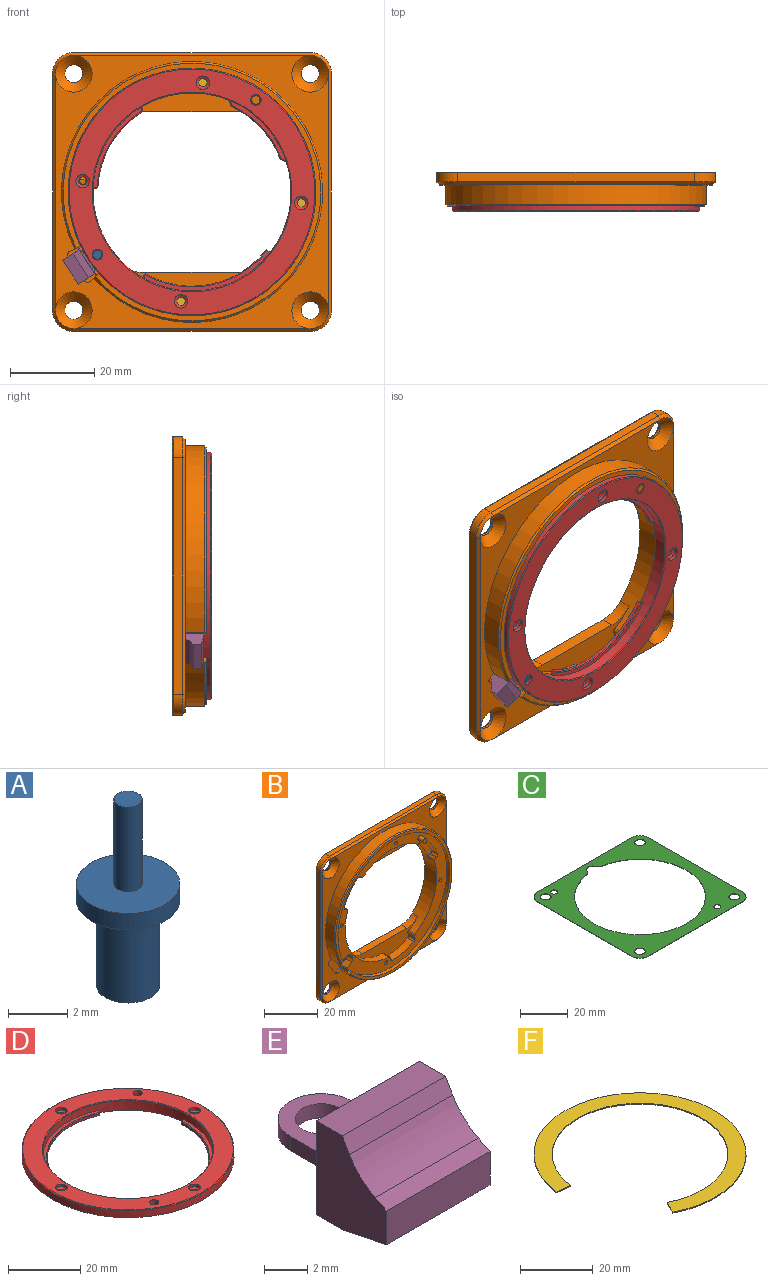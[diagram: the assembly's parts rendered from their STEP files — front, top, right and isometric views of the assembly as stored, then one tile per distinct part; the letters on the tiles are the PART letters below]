
ASSEMBLY  parts=6 mates=6
PART A: 7 faces, bbox 3.5x3.5x7.7 mm
  f0: cylinder r=1.07mm len=3.5mm, axis (0,0,-1), area 23.6mm2, adj f1,f4
  f1: plane 2.15x2.15mm, normal (0,0,-1), area 3.6mm2, adj f0
  f2: cylinder r=1.75mm len=3.5mm, axis (0,0,-1), area 7.5mm2, adj f3,f4
  f3: plane 3.5x3.5mm, normal (0,0,1), area 8.9mm2, adj f2,f5
  f4: plane 3.5x3.5mm, normal (0,0,-1), area 6mm2, adj f0,f2
  f5: cylinder r=0.47mm len=3.5mm, axis (0,0,-1), area 10.4mm2, adj f3,f6
  f6: plane 0.95x0.95mm, normal (0,0,1), area 0.7mm2, adj f5
PART B: 132 faces, bbox 66x9x66 mm
  f0: plane 66x66mm, normal (0,1,0), area 1941mm2, adj f7,f8,f9,f10,f11,f12,f13,f14
  f1: plane 64.6x64.6mm, normal (0,-1,0), area 904mm2, adj f2,f20,f21,f22,f23,f25,f26,f29
  f2: cylinder r=30.9mm len=61.8mm, axis (0,1,0), area 845.7mm2, adj f1,f54,f55,f84
  f3: plane 58.65x58.65mm, normal (0,-1,0), area 755.9mm2, adj f4,f5,f6,f40,f42,f44,f46,f48
  f4: cylinder r=24.05mm len=40.58mm, axis (0,1,0), area 255.6mm2, adj f3,f19,f33,f35,f37,f38,f67,f75
  f5: cylinder r=24.05mm len=37.04mm, axis (0,1,0), area 215.4mm2, adj f3,f19,f33,f35,f36,f39,f66,f70
  f6: cylinder r=24.05mm len=28.41mm, axis (0,1,0), area 100.3mm2, adj f3,f35,f72,f77
  f7: plane 56x2.15mm, normal (0,0,-1), area 120.4mm2, adj f0,f8,f14,f29
  f8: cylinder r=5mm len=5mm, axis (0,1,0), area 16.9mm2, adj f0,f7,f9,f31
  f9: plane 56x2.15mm, normal (1,0,0), area 120.4mm2, adj f0,f8,f10,f30
  f10: cylinder r=5mm len=5mm, axis (0,1,0), area 16.9mm2, adj f0,f9,f11,f28
  f11: plane 56x2.15mm, normal (0,0,1), area 120.4mm2, adj f0,f10,f12,f26
  f12: cylinder r=5mm len=5mm, axis (0,1,0), area 16.9mm2, adj f0,f11,f13,f24
  f13: plane 56x2.15mm, normal (-1,0,0), area 120.4mm2, adj f0,f12,f14,f25
  f14: cylinder r=5mm len=5mm, axis (0,1,0), area 16.9mm2, adj f0,f7,f13,f27
  f15: cylinder r=2.15mm len=4.3mm, axis (0,1,0), area 8.8mm2, adj f0,f22
  f16: cylinder r=2.15mm len=4.3mm, axis (0,1,0), area 8.8mm2, adj f0,f23
  f17: cylinder r=2.15mm len=4.3mm, axis (0,1,0), area 8.8mm2, adj f0,f20
  f18: cylinder r=2.15mm len=4.3mm, axis (0,1,0), area 8.8mm2, adj f0,f21
  f19: plane 49.6x39.6mm, normal (0,1,0), area 336.2mm2, adj f4,f5,f32,f34,f36,f37,f38,f39
  f20: cone r=2.15mm half-angle=45deg, axis (0,-1,0), area 63.3mm2, adj f1,f17,f29,f30,f31
  f21: cone r=4.35mm half-angle=45deg, axis (0,-1,0), area 63.3mm2, adj f1,f18,f25,f27,f29
  f22: cone r=2.15mm half-angle=45deg, axis (0,-1,0), area 63.3mm2, adj f1,f15,f24,f25,f26
  f23: cone r=4.35mm half-angle=45deg, axis (0,-1,0), area 63.3mm2, adj f1,f16,f26,f28,f30
  f24: cone r=4.3mm half-angle=45deg, axis (0,1,0), area 7mm2, adj f12,f22,f25,f26
  f25: plane 56.02x0.72mm, normal (-0.71,-0.71,0), area 55.4mm2, adj f1,f13,f21,f22,f24,f27
  f26: plane 56.02x0.72mm, normal (0,-0.71,0.71), area 55.4mm2, adj f1,f11,f22,f23,f24,f28
  f27: cone r=4.3mm half-angle=45deg, axis (0,1,0), area 7mm2, adj f14,f21,f25,f29
  f28: cone r=4.3mm half-angle=45deg, axis (0,1,0), area 7mm2, adj f10,f23,f26,f30
  f29: plane 56.02x0.72mm, normal (0,-0.71,-0.71), area 55.4mm2, adj f1,f7,f20,f21,f27,f31
  f30: plane 56.02x0.72mm, normal (0.71,-0.71,0), area 55.4mm2, adj f1,f9,f20,f23,f28,f31
  f31: cone r=4.3mm half-angle=45deg, axis (0,1,0), area 7mm2, adj f8,f20,f29,f30
  f32: plane 23.28x3mm, normal (0,0,1), area 69.8mm2, adj f19,f33,f36,f37
  f33: plane 34.89x9.93mm, normal (0,-1,0), area 134.9mm2, adj f4,f5,f32,f36,f37,f57,f58,f59
  f34: plane 23.28x3mm, normal (0,0,-1), area 69.8mm2, adj f19,f35,f38,f39
  f35: plane 49.03x16.61mm, normal (0,-1,0), area 169.4mm2, adj f4,f5,f6,f34,f38,f39,f60,f61
  f36: cylinder r=8mm len=5.8mm, axis (0,1,0), area 19.5mm2, adj f5,f19,f32,f33
  f37: cylinder r=8mm len=5.8mm, axis (0,1,0), area 19.5mm2, adj f4,f19,f32,f33
  f38: cylinder r=8mm len=5.8mm, axis (0,1,0), area 19.5mm2, adj f4,f19,f34,f35
  f39: cylinder r=8mm len=5.8mm, axis (0,1,0), area 19.5mm2, adj f5,f19,f34,f35
  f40: cylinder r=0.75mm len=3mm, axis (0,-1,0), area 14.1mm2, adj f3,f41
  f41: plane 1.5x1.5mm, normal (0,-1,0), area 1.8mm2, adj f40
  f42: cylinder r=0.75mm len=3mm, axis (0,-1,0), area 14.1mm2, adj f3,f43
  f43: plane 1.5x1.5mm, normal (0,-1,0), area 1.8mm2, adj f42
  f44: cylinder r=0.75mm len=3mm, axis (0,-1,0), area 14.1mm2, adj f3,f45
  f45: plane 1.5x1.5mm, normal (0,-1,0), area 1.8mm2, adj f44
  f46: cylinder r=0.75mm len=3mm, axis (0,-1,0), area 14.1mm2, adj f3,f47
  f47: plane 1.5x1.5mm, normal (0,-1,0), area 1.8mm2, adj f46
  f48: plane 4.2x2.21mm, normal (-0.62,0,0.78), area 11.9mm2, adj f3,f49,f79,f85
  f49: cylinder r=2mm len=4.2mm, axis (0,-1,0), area 12.5mm2, adj f3,f48,f50,f85
  f50: plane 4.2x0.53mm, normal (-0.83,0,-0.55), area 2.7mm2, adj f3,f49,f51,f85
  f51: cylinder r=2mm len=4.2mm, axis (0,-1,0), area 12.5mm2, adj f3,f50,f52,f85
  f52: plane 4.2x2.48mm, normal (0.48,0,-0.88), area 11.9mm2, adj f3,f51,f78,f85
  f53: plane 4.2x0.42mm, normal (-0.83,0,-0.55), area 2.1mm2, adj f3,f78,f81,f85
  f54: plane 5.7x2.46mm, normal (0.44,0,-0.9), area 5.2mm2, adj f1,f2,f3,f81,f82,f83,f84,f85
  f55: plane 5.7x2.05mm, normal (-0.66,0,0.75), area 5.2mm2, adj f1,f2,f3,f80,f82,f83,f84,f85
  f56: plane 4.2x0.42mm, normal (-0.83,0,-0.55), area 2.1mm2, adj f3,f79,f80,f85
  f57: plane 3.3x0.39mm, normal (-0.87,0,-0.49), area 1.5mm2, adj f3,f33,f66,f68
  f58: plane 3.3x0.45mm, normal (1,0,-0.01), area 1.5mm2, adj f3,f33,f67,f69
  f59: cylinder r=26.5mm len=11.34mm, axis (0,-1,0), area 38.9mm2, adj f3,f33,f68,f69
  f60: plane 3.3x0.42mm, normal (-0.35,0,0.94), area 1.5mm2, adj f3,f35,f70,f71
  f61: cylinder r=26.5mm len=10.15mm, axis (0,-1,0), area 42mm2, adj f3,f35,f71,f73
  f62: plane 3.3x0.36mm, normal (0.79,0,-0.61), area 1.5mm2, adj f3,f35,f72,f73
  f63: cylinder r=26.5mm len=9.5mm, axis (0,-1,0), area 38.9mm2, adj f3,f35,f74,f76
  f64: plane 3.3x0.42mm, normal (0.35,0,0.94), area 1.5mm2, adj f3,f35,f74,f75
  f65: plane 3.3x0.35mm, normal (-0.77,0,-0.63), area 1.5mm2, adj f3,f35,f76,f77
  f66: cylinder r=1mm len=3.3mm, axis (0,1,0), area 5.1mm2, adj f3,f5,f33,f57
  f67: cylinder r=1mm len=3.3mm, axis (0,1,0), area 5.1mm2, adj f3,f4,f33,f58
  f68: cylinder r=1mm len=3.3mm, axis (0,-1,0), area 5.3mm2, adj f3,f33,f57,f59
  f69: cylinder r=1mm len=3.3mm, axis (0,-1,0), area 5.3mm2, adj f3,f33,f58,f59
  f70: cylinder r=1mm len=3.3mm, axis (0,1,0), area 5.1mm2, adj f3,f5,f35,f60
  f71: cylinder r=1mm len=3.3mm, axis (0,-1,0), area 5.3mm2, adj f3,f35,f60,f61
  f72: cylinder r=1mm len=3.3mm, axis (0,1,0), area 5.1mm2, adj f3,f6,f35,f62
  f73: cylinder r=1mm len=3.3mm, axis (0,-1,0), area 5.3mm2, adj f3,f35,f61,f62
  f74: cylinder r=1mm len=3.3mm, axis (0,-1,0), area 5.3mm2, adj f3,f35,f63,f64
  f75: cylinder r=1mm len=3.3mm, axis (0,1,0), area 5.1mm2, adj f3,f4,f35,f64
  f76: cylinder r=1mm len=3.3mm, axis (0,-1,0), area 5.3mm2, adj f3,f35,f63,f65
  f77: cylinder r=1mm len=3.3mm, axis (0,1,0), area 5.1mm2, adj f3,f6,f35,f65
  f78: cylinder r=0.5mm len=4.2mm, axis (0,1,0), area 3.1mm2, adj f3,f52,f53,f85
  f79: cylinder r=0.5mm len=4.2mm, axis (0,1,0), area 3.1mm2, adj f3,f48,f56,f85
  f80: cylinder r=0.5mm len=4.2mm, axis (0,1,0), area 3mm2, adj f3,f55,f56,f85
  f81: cylinder r=0.5mm len=4.2mm, axis (0,-1,0), area 3mm2, adj f3,f53,f54,f85
  f82: cylinder r=29.32mm len=58.65mm, axis (0,1,0), area 264.6mm2, adj f3,f54,f55,f83
  f83: plane 61x61mm, normal (0,-1,0), area 211.4mm2, adj f54,f55,f82,f84
  f84: cone r=30.5mm half-angle=45deg, axis (0,1,0), area 104.5mm2, adj f2,f54,f55,f83
  f85: plane 9.41x8.93mm, normal (0,-1,0), area 45.7mm2, adj f48,f49,f50,f51,f52,f53,f54,f55
  f86: cylinder r=1mm len=1.45mm, axis (0,-1,0), area 1.3mm2, adj f1,f54,f85,f87
  f87: plane 5.48x3.63mm, normal (0.83,0,0.55), area 4.9mm2, adj f1,f85,f86,f88
  f88: cylinder r=1mm len=1.49mm, axis (0,-1,0), area 1.3mm2, adj f1,f55,f85,f87
  f89: cylinder r=0.55mm len=3.5mm, axis (0,-1,0), area 12.1mm2, adj f90,f131
  f90: plane 2.1x2.1mm, normal (0,-1,0), area 2.5mm2, adj f89,f91
  f91: cylinder r=1.05mm len=2.2mm, axis (0,-1,0), area 14.5mm2, adj f85,f90
  f92: cylinder r=1.5mm len=3mm, axis (0,1,0), area 10.4mm2, adj f0,f93
  f93: plane 3x3mm, normal (0,1,0), area 7.1mm2, adj f92
  f94: cylinder r=1.5mm len=3mm, axis (0,1,0), area 10.4mm2, adj f0,f95
  f95: plane 3x3mm, normal (0,1,0), area 7.1mm2, adj f94
  f96: plane 41x0.9mm, normal (0,0,-1), area 36.9mm2, adj f104,f109,f112,f123
  f97: plane 31x0.9mm, normal (-1,0,0), area 27.9mm2, adj f104,f109,f110,f127
  f98: plane 41x0.9mm, normal (0,0,1), area 36.9mm2, adj f104,f110,f111,f126
  f99: plane 41x0.9mm, normal (0,0,1), area 36.9mm2, adj f104,f105,f108,f114
  f100: plane 31x0.9mm, normal (-1,0,0), area 27.9mm2, adj f104,f105,f106,f115
  f101: plane 41x0.9mm, normal (0,0,-1), area 36.9mm2, adj f104,f106,f107,f119
  f102: plane 31x0.9mm, normal (1,0,0), area 27.9mm2, adj f104,f107,f108,f118
  f103: plane 31x0.9mm, normal (1,0,0), area 27.9mm2, adj f104,f111,f112,f122
  f104: plane 53x43mm, normal (0,1,0), area 230.9mm2, adj f96,f97,f98,f99,f100,f101,f102,f103
  f105: cylinder r=4.7mm len=4.7mm, axis (0,1,0), area 6.6mm2, adj f99,f100,f104,f113
  f106: cylinder r=4.7mm len=4.7mm, axis (0,-1,0), area 6.6mm2, adj f100,f101,f104,f117
  f107: cylinder r=4.7mm len=4.7mm, axis (0,1,0), area 6.6mm2, adj f101,f102,f104,f120
  f108: cylinder r=4.7mm len=4.7mm, axis (0,-1,0), area 6.6mm2, adj f99,f102,f104,f116
  f109: cylinder r=6mm len=6mm, axis (0,1,0), area 8.5mm2, adj f96,f97,f104,f125
  f110: cylinder r=6mm len=6mm, axis (0,-1,0), area 8.5mm2, adj f97,f98,f104,f128
  f111: cylinder r=6mm len=6mm, axis (0,1,0), area 8.5mm2, adj f98,f103,f104,f124
  f112: cylinder r=6mm len=6mm, axis (0,-1,0), area 8.5mm2, adj f96,f103,f104,f121
  f113: cone r=4.3mm half-angle=45deg, axis (0,-1,0), area 4mm2, adj f19,f105,f114,f115
  f114: plane 41x0.4mm, normal (0,0.71,0.71), area 23.2mm2, adj f19,f99,f113,f116
  f115: plane 31x0.4mm, normal (-0.71,0.71,0), area 17.5mm2, adj f19,f100,f113,f117
  f116: cone r=4.3mm half-angle=45deg, axis (0,-1,0), area 4mm2, adj f19,f108,f114,f118
  f117: cone r=4.3mm half-angle=45deg, axis (0,-1,0), area 4mm2, adj f19,f106,f115,f119
  f118: plane 31x0.4mm, normal (0.71,0.71,0), area 17.5mm2, adj f19,f102,f116,f120
  f119: plane 41x0.4mm, normal (0,0.71,-0.71), area 23.2mm2, adj f19,f101,f117,f120
  f120: cone r=4.3mm half-angle=45deg, axis (0,-1,0), area 4mm2, adj f19,f107,f118,f119
  f121: cone r=6.4mm half-angle=45deg, axis (0,1,0), area 5.5mm2, adj f0,f112,f122,f123
  f122: plane 31x0.4mm, normal (0.71,0.71,0), area 17.5mm2, adj f0,f103,f121,f124
  f123: plane 41x0.4mm, normal (0,0.71,-0.71), area 23.2mm2, adj f0,f96,f121,f125
  f124: cone r=6.4mm half-angle=45deg, axis (0,1,0), area 5.5mm2, adj f0,f111,f122,f126
  f125: cone r=6.4mm half-angle=45deg, axis (0,1,0), area 5.5mm2, adj f0,f109,f123,f127
  f126: plane 41x0.4mm, normal (0,0.71,0.71), area 23.2mm2, adj f0,f98,f124,f128
  f127: plane 31x0.4mm, normal (-0.71,0.71,0), area 17.5mm2, adj f0,f97,f125,f128
  f128: cone r=6.4mm half-angle=45deg, axis (0,1,0), area 5.5mm2, adj f0,f110,f126,f127
  f129: cylinder r=1mm len=2.7mm, axis (0,1,0), area 17mm2, adj f3,f130
  f130: plane 2x2mm, normal (0,-1,0), area 3.1mm2, adj f129
  f131: plane 1.1x1.1mm, normal (0,-1,0), area 1mm2, adj f89
PART C: 20 faces, bbox 65.9x65.9x0.2 mm
  f0: plane 55.9x0.15mm, normal (0,-1,0), area 8.4mm2, adj f1,f17,f18,f19
  f1: cylinder r=5mm len=5mm, axis (0,0,-1), area 1.2mm2, adj f0,f2,f18,f19
  f2: plane 55.9x0.15mm, normal (1,0,0), area 8.4mm2, adj f1,f3,f18,f19
  f3: cylinder r=5mm len=5mm, axis (0,0,-1), area 1.2mm2, adj f2,f4,f18,f19
  f4: plane 55.9x0.15mm, normal (0,1,0), area 8.4mm2, adj f3,f5,f18,f19
  f5: cylinder r=5mm len=5mm, axis (0,0,-1), area 1.2mm2, adj f4,f6,f18,f19
  f6: plane 55.9x0.15mm, normal (-1,0,0), area 8.4mm2, adj f5,f17,f18,f19
  f7: cylinder r=2.65mm len=4.76mm, axis (0,0,-1), area 0.9mm2, adj f8,f16,f18,f19
  f8: cylinder r=4mm len=2.83mm, axis (0,0,-1), area 0.6mm2, adj f7,f9,f18,f19
  f9: cylinder r=27.5mm len=55mm, axis (0,0,-1), area 24.3mm2, adj f8,f16,f18,f19
  f10: cylinder r=2.25mm len=4.5mm, axis (0,0,-1), area 2.1mm2, adj f18,f19
  f11: cylinder r=2.25mm len=4.5mm, axis (0,0,-1), area 2.1mm2, adj f18,f19
  f12: cylinder r=2.25mm len=4.5mm, axis (0,0,-1), area 2.1mm2, adj f18,f19
  f13: cylinder r=1.5mm len=3mm, axis (0,0,-1), area 1.4mm2, adj f18,f19
  f14: cylinder r=1.5mm len=3mm, axis (0,0,-1), area 1.4mm2, adj f18,f19
  f15: cylinder r=2.25mm len=4.5mm, axis (0,0,-1), area 2.1mm2, adj f18,f19
  f16: cylinder r=4mm len=2.83mm, axis (0,0,-1), area 0.6mm2, adj f7,f9,f18,f19
  f17: cylinder r=5mm len=5mm, axis (0,0,-1), area 1.2mm2, adj f0,f6,f18,f19
  f18: plane 65.9x65.9mm, normal (0,0,1), area 1851.8mm2, adj f0,f1,f2,f3,f4,f5,f6,f7
  f19: plane 65.9x65.9mm, normal (0,0,-1), area 1851.8mm2, adj f0,f1,f2,f3,f4,f5,f6,f7
PART D: 48 faces, bbox 58.6x58.6x3.4 mm
  f0: cylinder r=1.25mm len=2.5mm, axis (0,0,-1), area 14.9mm2, adj f9,f47
  f1: plane 58.6x58.6mm, normal (0,0,-1), area 827.8mm2, adj f2,f3,f4,f5,f7,f8,f22,f43
  f2: cylinder r=1mm len=2mm, axis (0,0,-1), area 7.8mm2, adj f1,f39
  f3: cylinder r=1mm len=2mm, axis (0,0,-1), area 7.8mm2, adj f1,f41
  f4: cylinder r=1mm len=2mm, axis (0,0,-1), area 7.8mm2, adj f1,f35
  f5: cylinder r=1mm len=2mm, axis (0,0,-1), area 7.8mm2, adj f1,f37
  f6: cylinder r=23.45mm len=46.9mm, axis (0,0,-1), area 401.1mm2, adj f10,f11,f12,f14,f15,f17,f18,f20
  f7: cylinder r=1.25mm len=2.5mm, axis (0,0,-1), area 19.6mm2, adj f1,f9
  f8: cylinder r=29.3mm len=58.6mm, axis (0,0,-1), area 418.6mm2, adj f1,f33,f44,f45,f47
  f9: plane 58.2x58.2mm, normal (0,0,1), area 861.2mm2, adj f0,f7,f33,f34,f36,f38,f40,f42
  f10: plane 29.17x11.36mm, normal (0,0,1), area 30.9mm2, adj f6,f27,f28,f29
  f11: plane 14.61x12.93mm, normal (0,0,1), area 17.9mm2, adj f6,f30,f31,f32
  f12: plane 20.42x9.69mm, normal (0,0,1), area 21.4mm2, adj f6,f24,f25,f26
  f13: cylinder r=22.3mm len=12.78mm, axis (0,0,1), area 12.3mm2, adj f14,f21,f23,f31
  f14: plane 1.43x0.7mm, normal (0.9,0.44,0), area 1.1mm2, adj f6,f13,f23,f30
  f15: plane 1.58x0.7mm, normal (-0.99,0.12,0), area 1.1mm2, adj f6,f16,f23,f25
  f16: cylinder r=22.3mm len=18.83mm, axis (0,0,1), area 15mm2, adj f15,f17,f23,f26
  f17: plane 1.13x0.7mm, normal (-0.31,0.95,0), area 0.8mm2, adj f6,f16,f23,f24
  f18: plane 1.05x0.7mm, normal (0.91,-0.41,0), area 0.8mm2, adj f6,f19,f23,f28
  f19: cylinder r=22.3mm len=28.02mm, axis (0,0,1), area 22.4mm2, adj f18,f20,f23,f29
  f20: plane 0.98x0.7mm, normal (-0.53,-0.85,0), area 0.8mm2, adj f6,f19,f23,f27
  f21: plane 1.5x0.7mm, normal (0.33,0.95,0), area 1.1mm2, adj f6,f13,f23,f32
  f22: cylinder r=24mm len=48mm, axis (0,0,1), area 139.8mm2, adj f1,f23,f43,f46,f47
  f23: plane 48x48mm, normal (0,0,-1), area 167.8mm2, adj f6,f13,f14,f15,f16,f17,f18,f19
  f24: cylinder r=0.2mm len=1.19mm, axis (0.95,0.31,0), area 0.4mm2, adj f6,f12,f17,f26
  f25: cylinder r=0.2mm len=1.6mm, axis (0.12,0.99,0), area 0.5mm2, adj f6,f12,f15,f26
  f26: torus R=22.5mm, axis (0,0,-1), area 6.7mm2, adj f12,f16,f24,f25
  f27: cylinder r=0.2mm len=1.08mm, axis (-0.85,0.53,0), area 0.3mm2, adj f6,f10,f20,f29
  f28: cylinder r=0.2mm len=1.13mm, axis (-0.41,-0.91,0), area 0.3mm2, adj f6,f10,f18,f29
  f29: torus R=22.5mm, axis (0,0,-1), area 10mm2, adj f10,f19,f27,f28
  f30: cylinder r=0.2mm len=1.52mm, axis (0.44,-0.9,0), area 0.5mm2, adj f6,f11,f14,f31
  f31: torus R=22.5mm, axis (0,0,-1), area 5.5mm2, adj f11,f13,f30,f32
  f32: cylinder r=0.2mm len=1.57mm, axis (0.95,-0.33,0), area 0.5mm2, adj f6,f11,f21,f31
  f33: cone r=29.1mm half-angle=45deg, axis (0,0,-1), area 51.9mm2, adj f8,f9
  f34: cone r=23.45mm half-angle=45deg, axis (0,0,1), area 41.9mm2, adj f6,f9
  f35: cone r=0mm half-angle=59deg, axis (0,0,1), area 5.7mm2, adj f4,f36
  f36: cylinder r=1.6mm len=3.2mm, axis (0,0,1), area 9mm2, adj f9,f35
  f37: cone r=0mm half-angle=59deg, axis (0,0,1), area 5.7mm2, adj f5,f38
  f38: cylinder r=1.6mm len=3.2mm, axis (0,0,1), area 9mm2, adj f9,f37
  f39: cone r=0mm half-angle=59deg, axis (0,0,1), area 5.7mm2, adj f2,f40
  f40: cylinder r=1.6mm len=3.2mm, axis (0,0,1), area 9mm2, adj f9,f39
  f41: cone r=0mm half-angle=59deg, axis (0,0,1), area 5.7mm2, adj f3,f42
  f42: cylinder r=1.6mm len=3.2mm, axis (0,0,1), area 9mm2, adj f9,f41
  f43: cylinder r=1mm len=1.03mm, axis (0,0,-1), area 0.7mm2, adj f1,f22,f44,f47
  f44: plane 3.38x2.76mm, normal (0.63,-0.77,0), area 2.6mm2, adj f1,f8,f43,f47
  f45: plane 3.38x2.76mm, normal (-0.63,0.77,0), area 2.6mm2, adj f1,f8,f46,f47
  f46: cylinder r=1mm len=1.07mm, axis (0,0,-1), area 0.7mm2, adj f1,f22,f45,f47
  f47: plane 9.18x8.81mm, normal (0,0,-1), area 37.3mm2, adj f0,f8,f22,f43,f44,f45,f46
PART E: 16 faces, bbox 6.7x9.6x5.3 mm
  f0: cylinder r=2mm len=4mm, axis (0,0,-1), area 5mm2, adj f1,f3,f4,f5
  f1: plane 3x0.8mm, normal (-1,0,0), area 2.4mm2, adj f0,f4,f5,f8
  f2: cylinder r=1.2mm len=2.4mm, axis (0,0,-1), area 6mm2, adj f4,f5
  f3: plane 3x0.8mm, normal (1,0,0), area 2.4mm2, adj f0,f4,f5,f8
  f4: plane 5x4mm, normal (0,0,1), area 13.8mm2, adj f0,f1,f2,f3,f8
  f5: plane 5x4mm, normal (0,0,-1), area 13.8mm2, adj f0,f1,f2,f3,f8
  f6: plane 6.73x0.83mm, normal (0,-0.87,0.5), area 6.4mm2, adj f7,f13,f14,f15
  f7: plane 6.73x1.7mm, normal (0,0,1), area 11.4mm2, adj f6,f8,f14,f15
  f8: plane 6.73x5.3mm, normal (0,1,0), area 32.5mm2, adj f1,f3,f4,f5,f7,f9,f14,f15
  f9: plane 6.73x1.7mm, normal (0,0,-1), area 11.4mm2, adj f8,f10,f14,f15
  f10: plane 6.73x2.9mm, normal (0,-0.2,-0.98), area 19.9mm2, adj f9,f11,f14,f15
  f11: plane 6.73x1.9mm, normal (0,-1,0), area 12.8mm2, adj f10,f12,f14,f15
  f12: plane 6.73x0.76mm, normal (0,-0.45,0.89), area 5.8mm2, adj f11,f13,f14,f15
  f13: cylinder r=4mm len=6.73mm, axis (1,0,0), area 15.7mm2, adj f6,f12,f14,f15
  f14: plane 5.3x4.6mm, normal (-1,0,0), area 18.4mm2, adj f6,f7,f8,f9,f10,f11,f12,f13
  f15: plane 5.3x4.6mm, normal (1,0,0), area 18.4mm2, adj f6,f7,f8,f9,f10,f11,f12,f13
PART F: 6 faces, bbox 58.3x58.5x0.3 mm
  f0: plane 4.45x2.27mm, normal (-0.89,0.45,0), area 1.5mm2, adj f1,f3,f4,f5
  f1: cylinder r=29.25mm len=58.5mm, axis (0,0,-1), area 44.5mm2, adj f0,f2,f4,f5
  f2: plane 4.97x0.58mm, normal (-0.12,-0.99,0), area 1.5mm2, adj f1,f3,f4,f5
  f3: cylinder r=24.25mm len=48.5mm, axis (0,0,-1), area 36.9mm2, adj f0,f2,f4,f5
  f4: plane 58.5x58.3mm, normal (0,0,1), area 677.8mm2, adj f0,f1,f2,f3
  f5: plane 58.5x58.3mm, normal (0,0,-1), area 677.8mm2, adj f0,f1,f2,f3
PLACE A rot(axis=(-1,0,0),90deg) t=(-18.47,-2.42,-15.82)mm
PLACE B t=(3.93,6.06,-0.97)mm fixed
PLACE C rot(axis=(1,0,0),90deg) t=(-29.07,6.21,32.03)mm
PLACE D rot(axis=(0.04,-0.71,0.71),176deg) t=(3.93,-0.54,-0.97)mm
PLACE E rot(axis=(-0.35,-0.66,-0.66),140.9deg) t=(-18.47,0.28,-15.82)mm
PLACE F rot(axis=(1,0,0),90deg) t=(3.93,-0.24,-0.97)mm
MATE revolute B.f42 <-> D.f2  axis (0,-1,0) through (1.35,-0.24,-26.84)mm
MATE revolute A.f0 <-> E.f2  axis (0,-1,0) through (-18.47,1.08,-15.82)mm
MATE fastened C.f9 <-> B.f2  axis (0,-1,0) through (3.93,6.06,-0.97)mm
MATE fastened B.f2 <-> F.f3  axis (0,-1,0) through (3.93,-0.24,-0.97)mm
MATE revolute B.f46 <-> D.f4  axis (0,-1,0) through (6.51,-0.24,24.9)mm
MATE fastened A.f2 <-> B.f89  axis (0,1,0) through (-18.47,1.76,-15.82)mm
